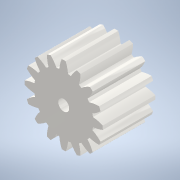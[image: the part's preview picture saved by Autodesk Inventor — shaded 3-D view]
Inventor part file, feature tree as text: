
AUTODESK INVENTOR PART (.ipt)
format: ipt  version: 2020.3 (Build 243373000, 373)  size: 215,552 bytes
history: native  units: mm (DEFAULTED — no unit token found)
features: plane x3, other x3, sketch x3, extrude x2
ambient origin geometry x8: Origin, YZ Plane, XZ Plane, XY Plane, X Axis, Y Axis, Z Axis, Center Point
bodies: Solid1 (feature_tree)
feature tree (11):
  extrude  "Extrusion1"  Depth=48.0mm TaperAngle=0.0deg
  plane  "Work Plane2"
  plane  "Work Plane8"
  plane  "Work Plane9"
  other  "Spur Gear"
  extrude  "Extrusion2"  Depth=10.0mm TaperAngle=0.0deg
  sketch  "Sketch1"  dims[d0=71.400418mm d1=48.0mm d2=0.0mm]
  sketch  "Sketch2"  dims[d3=65.361702mm d4=10.0mm d5=0.0mm]
  other  "Srf1"
  sketch  "Sketch3"  dims[d16=192.0mm d17=0.0mm d34=1.963495mm d39=0.0mm d41=0.0mm d43=192.0mm d46=192.0mm d47=0.0mm d48=0.0mm d49=10.0mm d50=48.0mm d51=0.0mm]
  other  "Pitch Diameter"
